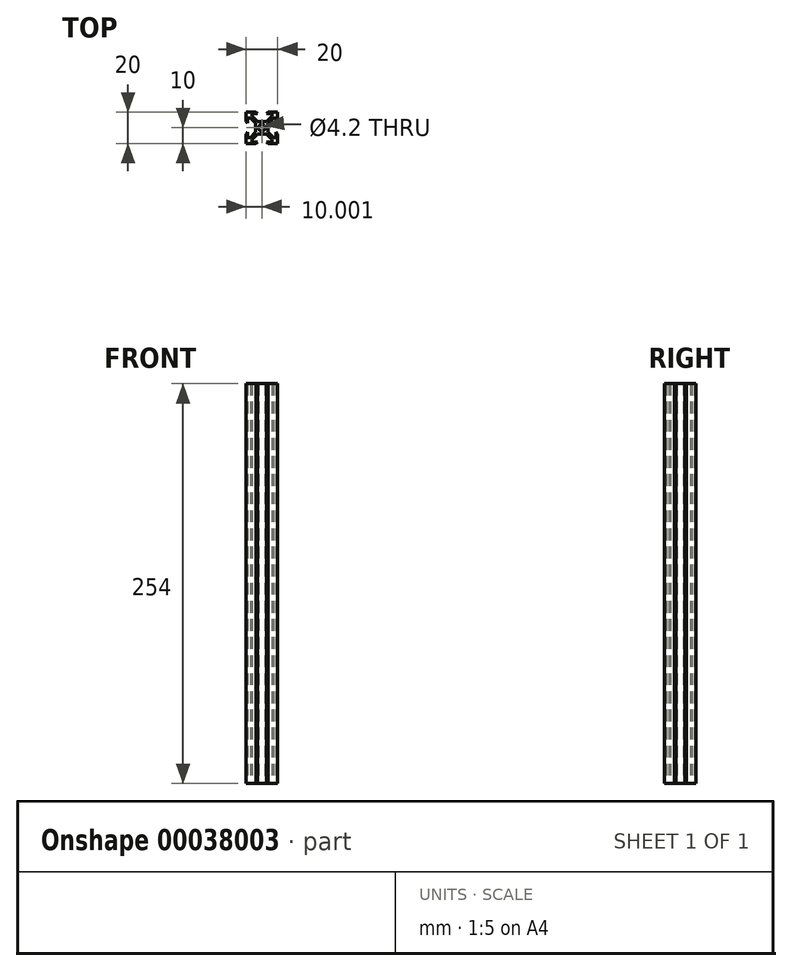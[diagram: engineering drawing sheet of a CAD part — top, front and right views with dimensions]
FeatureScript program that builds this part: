
annotation { "Feature Type Name" : "Feature", "Feature Type Description" : "" }
export const myFeature = defineFeature(function(context is Context, id is Id, definition is map)
    precondition{}
    {
        {
            var Q0;
            Q0=qCreatedBy(makeId("Top.planeOp"),FACE);
            var sketch = newSketch(context, id + "F0", { "sketchPlane" : qUnion([Q0])});
            skLineSegment(sketch, "E0", {"start": v(0, 0) * mm, "end": v(0, -5.68) * mm});
            skLineSegment(sketch, "E1", {"start": v(0, -2.84) * mm, "end": v(7.8, -2.84) * mm, "construction": true});
            skLineSegment(sketch, "E2", {"start": v(3.9, 1.06) * mm, "end": v(3.9, -6.74) * mm, "construction": true});
            skLineSegment(sketch, "E3", {"start": v(0, 0) * mm, "end": v(1.06, 1.06) * mm, "construction": true});
            skLineSegment(sketch, "E4", {"start": v(0, -5.68) * mm, "end": v(1.06, -6.74) * mm, "construction": true});
            skLineSegment(sketch, "E5", {"start": v(1.06, 1.06) * mm, "end": v(6.74, 1.06) * mm});
            skLineSegment(sketch, "E6", {"start": v(7.8, 0) * mm, "end": v(7.8, -5.68) * mm});
            skLineSegment(sketch, "E7", {"start": v(1.06, -6.74) * mm, "end": v(6.74, -6.74) * mm});
            skCircle(sketch, "E8", {"center": v(3.9, -2.84) * mm, "radius": 2.1 * mm});
            skLineSegment(sketch, "E9", {"start": v(6.74, 1.06) * mm, "end": v(7.8, 0) * mm, "construction": true});
            skLineSegment(sketch, "E10", {"start": v(7.8, -5.68) * mm, "end": v(6.74, -6.74) * mm, "construction": true});
            skLineSegment(sketch, "E11", {"start": v(6.74, 1.06) * mm, "end": v(10.2, 4.52) * mm});
            skLineSegment(sketch, "E12", {"start": v(7.8, 0) * mm, "end": v(11.26, 3.46) * mm});
            skLineSegment(sketch, "E13", {"start": v(7.8, -5.68) * mm, "end": v(11.26, -9.14) * mm});
            skLineSegment(sketch, "E14", {"start": v(6.74, -6.74) * mm, "end": v(10.2, -10.2) * mm});
            skLineSegment(sketch, "E15", {"start": v(1.06, -6.74) * mm, "end": v(-2.4, -10.2) * mm});
            skLineSegment(sketch, "E16", {"start": v(0, -5.68) * mm, "end": v(-3.46, -9.14) * mm});
            skLineSegment(sketch, "E17", {"start": v(0, 0) * mm, "end": v(-3.46, 3.46) * mm});
            skLineSegment(sketch, "E18", {"start": v(1.06, 1.06) * mm, "end": v(-2.4, 4.52) * mm});
            skLineSegment(sketch, "E19", {"start": v(-2.4, 4.52) * mm, "end": v(-2.4, 6.16) * mm});
            skLineSegment(sketch, "E20", {"start": v(10.2, 4.52) * mm, "end": v(10.2, 6.16) * mm});
            skLineSegment(sketch, "E21", {"start": v(-3.46, 3.46) * mm, "end": v(-5.1, 3.46) * mm});
            skLineSegment(sketch, "E22", {"start": v(-3.46, -9.14) * mm, "end": v(-5.1, -9.14) * mm});
            skLineSegment(sketch, "E23", {"start": v(-2.4, -10.2) * mm, "end": v(-2.4, -11.84) * mm});
            skLineSegment(sketch, "E24", {"start": v(10.2, -10.2) * mm, "end": v(10.2, -11.84) * mm});
            skLineSegment(sketch, "E25", {"start": v(11.26, -9.14) * mm, "end": v(12.9, -9.14) * mm});
            skLineSegment(sketch, "E26", {"start": v(11.26, 3.46) * mm, "end": v(12.9, 3.46) * mm});
            skLineSegment(sketch, "E27", {"start": v(10.2, -11.84) * mm, "end": v(6.74, -11.84) * mm});
            skLineSegment(sketch, "E28", {"start": v(-2.4, -11.84) * mm, "end": v(1.06, -11.84) * mm});
            skLineSegment(sketch, "E29", {"start": v(-5.1, -9.14) * mm, "end": v(-5.1, -5.68) * mm});
            skLineSegment(sketch, "E30", {"start": v(-5.1, 3.46) * mm, "end": v(-5.1, 0) * mm});
            skLineSegment(sketch, "E31", {"start": v(-2.4, 6.16) * mm, "end": v(1.06, 6.16) * mm});
            skLineSegment(sketch, "E32", {"start": v(10.2, 6.16) * mm, "end": v(6.74, 6.16) * mm});
            skLineSegment(sketch, "E33", {"start": v(12.9, 3.46) * mm, "end": v(12.9, 0) * mm});
            skLineSegment(sketch, "E34", {"start": v(12.9, -9.14) * mm, "end": v(12.9, -5.68) * mm});
            skLineSegment(sketch, "E35", {"start": v(1.06, 6.16) * mm, "end": v(6.74, 6.16) * mm, "construction": true});
            skLineSegment(sketch, "E36", {"start": v(3.9, 6.16) * mm, "end": v(3.9, 7.16) * mm, "construction": true});
            skLineSegment(sketch, "E37", {"start": v(0.06, 7.16) * mm, "end": v(7.74, 7.16) * mm, "construction": true});
            skLineSegment(sketch, "E38", {"start": v(6.74, 6.16) * mm, "end": v(7.74, 7.16) * mm});
            skLineSegment(sketch, "E39", {"start": v(1.06, 6.16) * mm, "end": v(0.06, 7.16) * mm});
            skLineSegment(sketch, "E40", {"start": v(7.74, 7.16) * mm, "end": v(13.9, 7.16) * mm});
            skLineSegment(sketch, "E41", {"start": v(13.9, 7.16) * mm, "end": v(13.9, 1) * mm});
            skLineSegment(sketch, "E42", {"start": v(12.9, 0) * mm, "end": v(13.9, 1) * mm});
            skLineSegment(sketch, "E43", {"start": v(0.06, 7.16) * mm, "end": v(-6.1, 7.16) * mm});
            skLineSegment(sketch, "E44", {"start": v(-6.1, 7.16) * mm, "end": v(-6.1, 1) * mm});
            skLineSegment(sketch, "E45", {"start": v(-6.1, 1) * mm, "end": v(-5.1, 0) * mm});
            skLineSegment(sketch, "E46", {"start": v(-5.1, -5.68) * mm, "end": v(-6.1, -6.68) * mm});
            skLineSegment(sketch, "E47", {"start": v(-6.1, -6.68) * mm, "end": v(-6.1, -12.84) * mm});
            skLineSegment(sketch, "E48", {"start": v(-6.1, -12.84) * mm, "end": v(0.06, -12.84) * mm});
            skLineSegment(sketch, "E49", {"start": v(0.06, -12.84) * mm, "end": v(1.06, -11.84) * mm});
            skLineSegment(sketch, "E50", {"start": v(6.74, -11.84) * mm, "end": v(7.74, -12.84) * mm});
            skLineSegment(sketch, "E51", {"start": v(7.74, -12.84) * mm, "end": v(13.9, -12.84) * mm});
            skLineSegment(sketch, "E52", {"start": v(13.9, -12.84) * mm, "end": v(13.9, -6.68) * mm});
            skLineSegment(sketch, "E53", {"start": v(12.9, -5.68) * mm, "end": v(13.9, -6.68) * mm});
            skLineSegment(sketch, "E54", {"start": v(-6.1, 1) * mm, "end": v(-6.1, -6.68) * mm, "construction": true});
            skLineSegment(sketch, "E55", {"start": v(0.06, -12.84) * mm, "end": v(7.74, -12.84) * mm, "construction": true});
            skLineSegment(sketch, "E56", {"start": v(13.9, -6.68) * mm, "end": v(13.9, 1) * mm, "construction": true});
            skSolve(sketch);
        }
        {
            var Q0;
            Q0=qSketchRegion(id+"F0",true);
            extrude(context, id + "F1", {"entities" : qUnion([Q0]), "depth" : 254 * mm});
        }
    });
